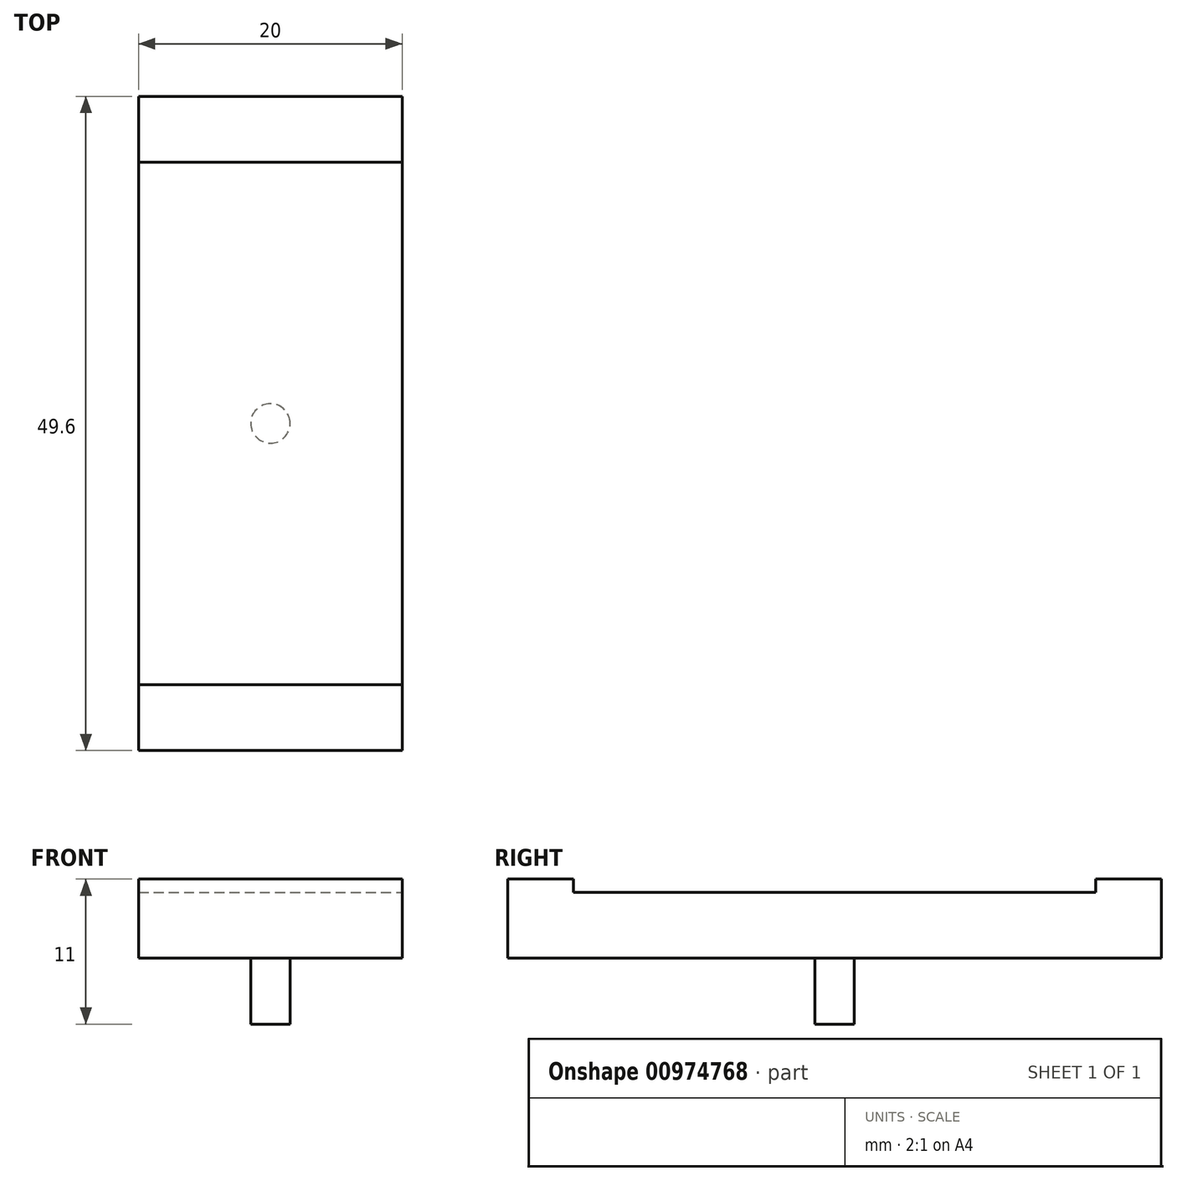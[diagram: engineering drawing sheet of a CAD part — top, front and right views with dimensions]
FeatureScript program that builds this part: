
annotation { "Feature Type Name" : "Feature", "Feature Type Description" : "" }
export const myFeature = defineFeature(function(context is Context, id is Id, definition is map)
    precondition{}
    {
        {
            var Q0;
            Q0=qCreatedBy(makeId("Top.planeOp"),FACE);
            var sketch = newSketch(context, id + "F0", { "sketchPlane" : qUnion([Q0])});
            skCircle(sketch, "E0", {"center": v(0, 0) * mm, "radius": 1.5 * mm});
            skSolve(sketch);
        }
        {
            var Q0;
            Q0 = qSketchRegion(id + "F0", true);
            extrude(context, id + "F1", {"entities" : qUnion([Q0]), "oppositeDirection" : true, "depth" : 5 * mm, "offsetDistance" : 25 * mm});
        }
        {
            var Q0;
            Q0=qCreatedBy(makeId("Top.planeOp"),FACE);
            var sketch = newSketch(context, id + "F2", { "sketchPlane" : qUnion([Q0])});
            skLineSegment(sketch, "E1.bottom", {"start": v(19.8, 10) * mm, "end": v(-19.8, 10) * mm});
            skLineSegment(sketch, "E1.top", {"start": v(19.8, -10) * mm, "end": v(-19.8, -10) * mm});
            skLineSegment(sketch, "E1.left", {"start": v(19.8, 10) * mm, "end": v(19.8, -10) * mm});
            skLineSegment(sketch, "E1.right", {"start": v(-19.8, 10) * mm, "end": v(-19.8, -10) * mm});
            skPoint(sketch, "E1.middle", {"position": v(0, 0) * mm});
            skLineSegment(sketch, "E2.bottom", {"start": v(-19.8, 10) * mm, "end": v(-24.8, 10) * mm});
            skLineSegment(sketch, "E2.top", {"start": v(-19.8, -10) * mm, "end": v(-24.8, -10) * mm});
            skLineSegment(sketch, "E2.right", {"start": v(-24.8, 10) * mm, "end": v(-24.8, -10) * mm});
            skLineSegment(sketch, "E3.bottom", {"start": v(19.8, 10) * mm, "end": v(24.8, 10) * mm});
            skLineSegment(sketch, "E3.top", {"start": v(19.8, -10) * mm, "end": v(24.8, -10) * mm});
            skLineSegment(sketch, "E3.right", {"start": v(24.8, 10) * mm, "end": v(24.8, -10) * mm});
            skSolve(sketch);
        }
        {
            var Q0;
            Q0=makeQuery(id+"F2.imprint","IMPRINT",FACE,{"disambiguationData":[TD([[makeQuery(id+"F2.imprint","IMPRINT",EDGE,{"derivedFrom":sQuery(id+"F2.wireOp",EDGE,"E1.bottom")}),1.0]])]});
            extrude(context, id + "F3", {"entities" : qUnion([Q0]), "operationType" : NewBodyOperationType.ADD, "depth" : 5 * mm, "offsetDistance" : 25 * mm});
        }
        {
            var Q0;
            Q0=makeQuery(id+"F2.imprint","IMPRINT",FACE,{"disambiguationData":[TD([[makeQuery(id+"F2.imprint","IMPRINT",EDGE,{"derivedFrom":sQuery(id+"F2.wireOp",EDGE,"E2.bottom")}),1.0]])]});
            var Q1;
            Q1=makeQuery(id+"F2.imprint","IMPRINT",FACE,{"disambiguationData":[TD([[makeQuery(id+"F2.imprint","IMPRINT",EDGE,{"derivedFrom":sQuery(id+"F2.wireOp",EDGE,"E3.bottom")}),-1.0]])]});
            extrude(context, id + "F4", {"entities" : qUnion([Q0, Q1]), "operationType" : NewBodyOperationType.ADD, "depth" : 6 * mm, "offsetDistance" : 25 * mm});
        }
        {
            var Q0;
            Q0=makeQuery(id+"F1.opExtrude","SWEPT_BODY",BODY,{"disambiguationData":[OSD([sQuery(id+"F0.wireOp",EDGE,"E0")])]});
            var Q1;
            Q1=makeQuery(id+"F1.opExtrude","CAP_EDGE",EDGE,{"disambiguationData":[OSD([sQuery(id+"F0.wireOp",EDGE,"E0")])],"isStart":false});
            transform(context, id + "F5", {"entities" : qUnion([Q0]), "transformType" : TransformType.ROTATION, "transformAxis" : qUnion([Q1]), "angle" : 90 * degree, "makeCopy" : false});
        }
    });
